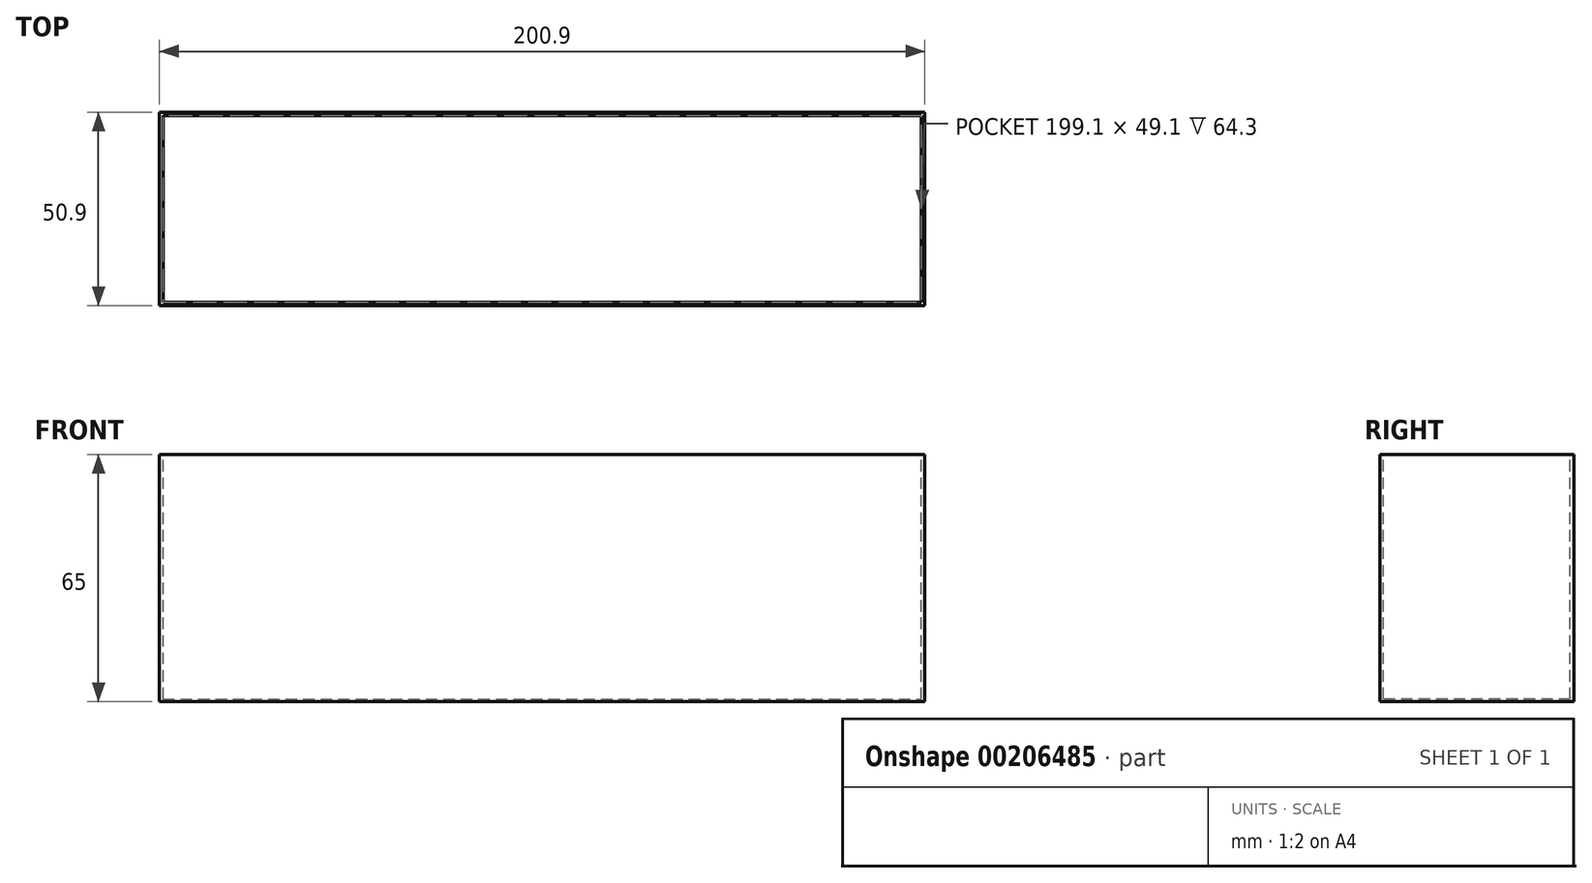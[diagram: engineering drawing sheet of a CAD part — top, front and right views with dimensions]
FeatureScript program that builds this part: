
annotation { "Feature Type Name" : "Feature", "Feature Type Description" : "" }
export const myFeature = defineFeature(function(context is Context, id is Id, definition is map)
    precondition{}
    {
        {
            var Q0;
            Q0=qCreatedBy(makeId("Top.planeOp"),FACE);
            var sketch = newSketch(context, id + "F0", { "sketchPlane" : qUnion([Q0])});
            skLineSegment(sketch, "E0.bottom", {"start": v(0, 0) * mm, "end": v(200.9, 0) * mm});
            skLineSegment(sketch, "E0.top", {"start": v(0, 50.9) * mm, "end": v(200.9, 50.9) * mm});
            skLineSegment(sketch, "E0.left", {"start": v(0, 0) * mm, "end": v(0, 50.9) * mm});
            skLineSegment(sketch, "E0.right", {"start": v(200.9, 0) * mm, "end": v(200.9, 50.9) * mm});
            skSolve(sketch);
        }
        {
            var Q0;
            Q0 = qSketchRegion(id + "F0", true);
            extrude(context, id + "F1", {"entities" : qUnion([Q0]), "depth" : 65 * mm, "offsetDistance" : 25 * mm});
        }
        {
            var Q0;
            Q0=makeQuery(id+"F1.opExtrude","CAP_FACE",FACE,{"disambiguationData":[OSD([sQuery(id+"F0.wireOp",EDGE,"E0.bottom"),sQuery(id+"F0.wireOp",EDGE,"E0.top"),sQuery(id+"F0.wireOp",EDGE,"E0.left"),sQuery(id+"F0.wireOp",EDGE,"E0.right")])],"isStart":false});
            var sketch = newSketch(context, id + "F2", { "sketchPlane" : qUnion([Q0])});
            skLineSegment(sketch, "E1.bottom", {"start": v(0.9, 50) * mm, "end": v(200, 50) * mm});
            skLineSegment(sketch, "E1.top", {"start": v(0.9, 0.9) * mm, "end": v(200, 0.9) * mm});
            skLineSegment(sketch, "E1.left", {"start": v(0.9, 50) * mm, "end": v(0.9, 0.9) * mm});
            skLineSegment(sketch, "E1.right", {"start": v(200, 50) * mm, "end": v(200, 0.9) * mm});
            skSolve(sketch);
        }
        {
            var Q0;
            Q0=makeQuery(id+"F2.imprint","IMPRINT",FACE,{"disambiguationData":[TD([[makeQuery(id+"F2.imprint","IMPRINT",EDGE,{"derivedFrom":sQuery(id+"F2.wireOp",EDGE,"E1.bottom")}),-1.0]])]});
            extrude(context, id + "F3", {"entities" : qUnion([Q0]), "operationType" : NewBodyOperationType.REMOVE, "oppositeDirection" : true, "depth" : 64.3 * mm, "offsetDistance" : 25 * mm});
        }
    });
